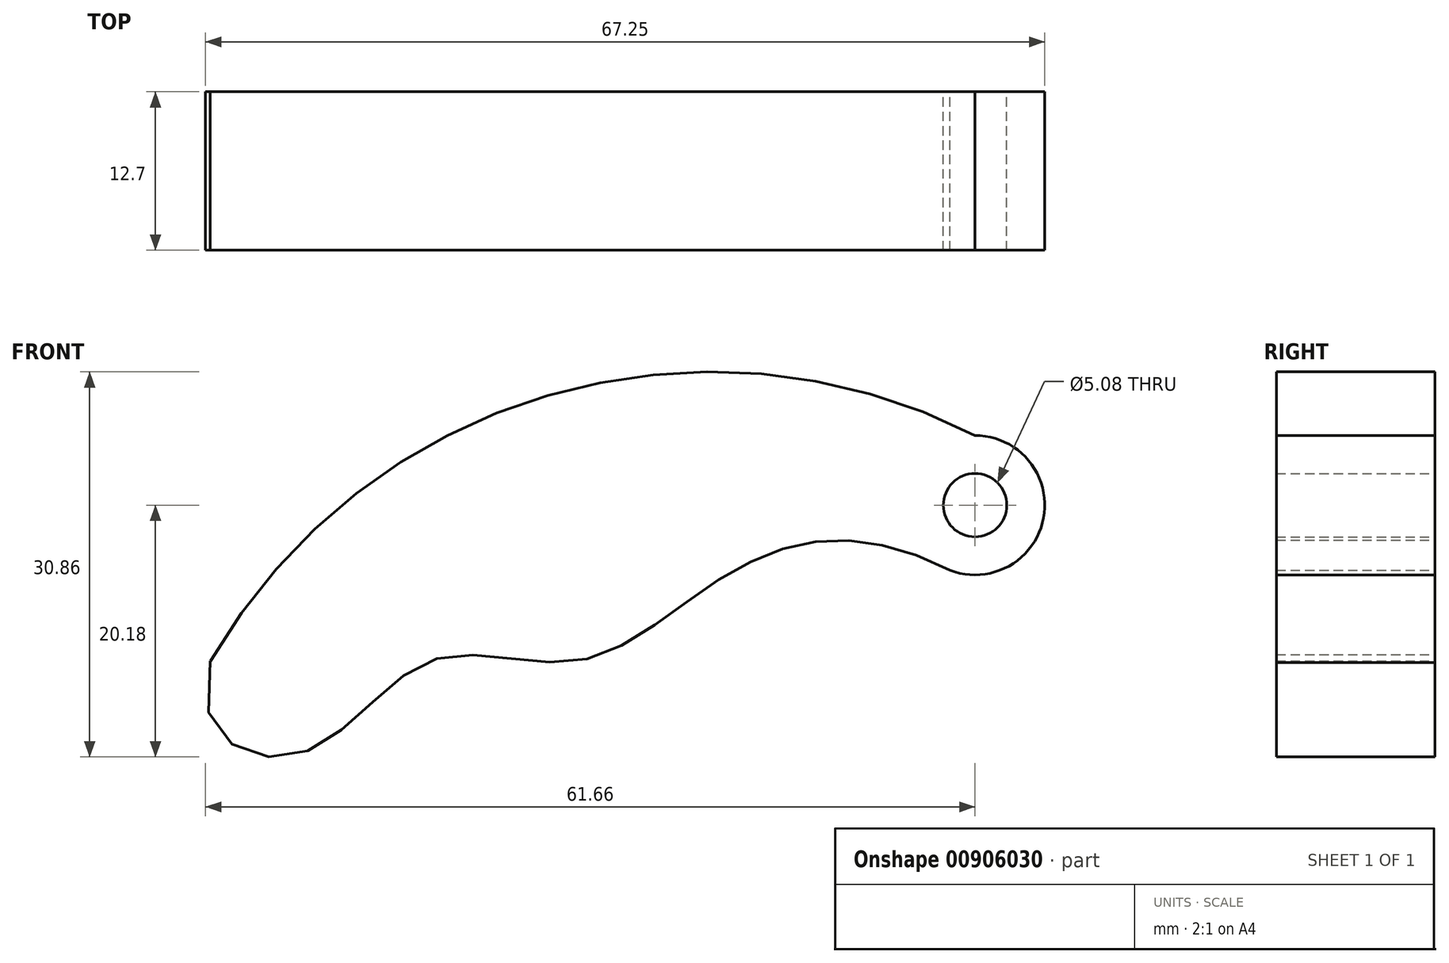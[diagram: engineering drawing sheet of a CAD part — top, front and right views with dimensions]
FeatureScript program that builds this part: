
annotation { "Feature Type Name" : "Feature", "Feature Type Description" : "" }
export const myFeature = defineFeature(function(context is Context, id is Id, definition is map)
    precondition{}
    {
        {
            var Q0;
            Q0=qCreatedBy(makeId("Front.planeOp"),FACE);
            var sketch = newSketch(context, id + "F0", { "sketchPlane" : qUnion([Q0])});
            skArc(sketch, "E0", {"start": v(-2.01, -5.21) * mm, "mid": v(5.5, -1.02) * mm, "end": v(0, 5.59) * mm});
            skArc(sketch, "E1", {"start": v(0, 5.59) * mm, "mid": v(-34.25, 8.79) * mm, "end": v(-61.27, -12.49) * mm});
            skFitSpline(sketch, "E2", {"points": [v(-61.27, -12.49) * mm, v(-54.59, -20.03) * mm, v(-43.7, -12.49) * mm, v(-31.9, -12.49) * mm, v(-21.23, -6.41) * mm, v(-11.8, -2.84) * mm, v(-2.01, -5.21) * mm], "startDerivative": vector(-33.8, -113.5) * mm, "endDerivative": vector(62.2, -31.66) * mm});
            skCircle(sketch, "E3", {"center": v(0, 0) * mm, "radius": 2.54 * mm});
            skSolve(sketch);
        }
        {
            var Q0;
            Q0=makeQuery(id+"F0.imprint","IMPRINT",FACE,{"disambiguationData":[TD([[makeQuery(id+"F0.imprint","IMPRINT",EDGE,{"derivedFrom":sQuery(id+"F0.wireOp",EDGE,"E0")}),1.0]])]});
            extrude(context, id + "F1", {"entities" : qUnion([Q0]), "depth" : 12.7 * mm, "offsetDistance" : 25.4 * mm});
        }
    });
